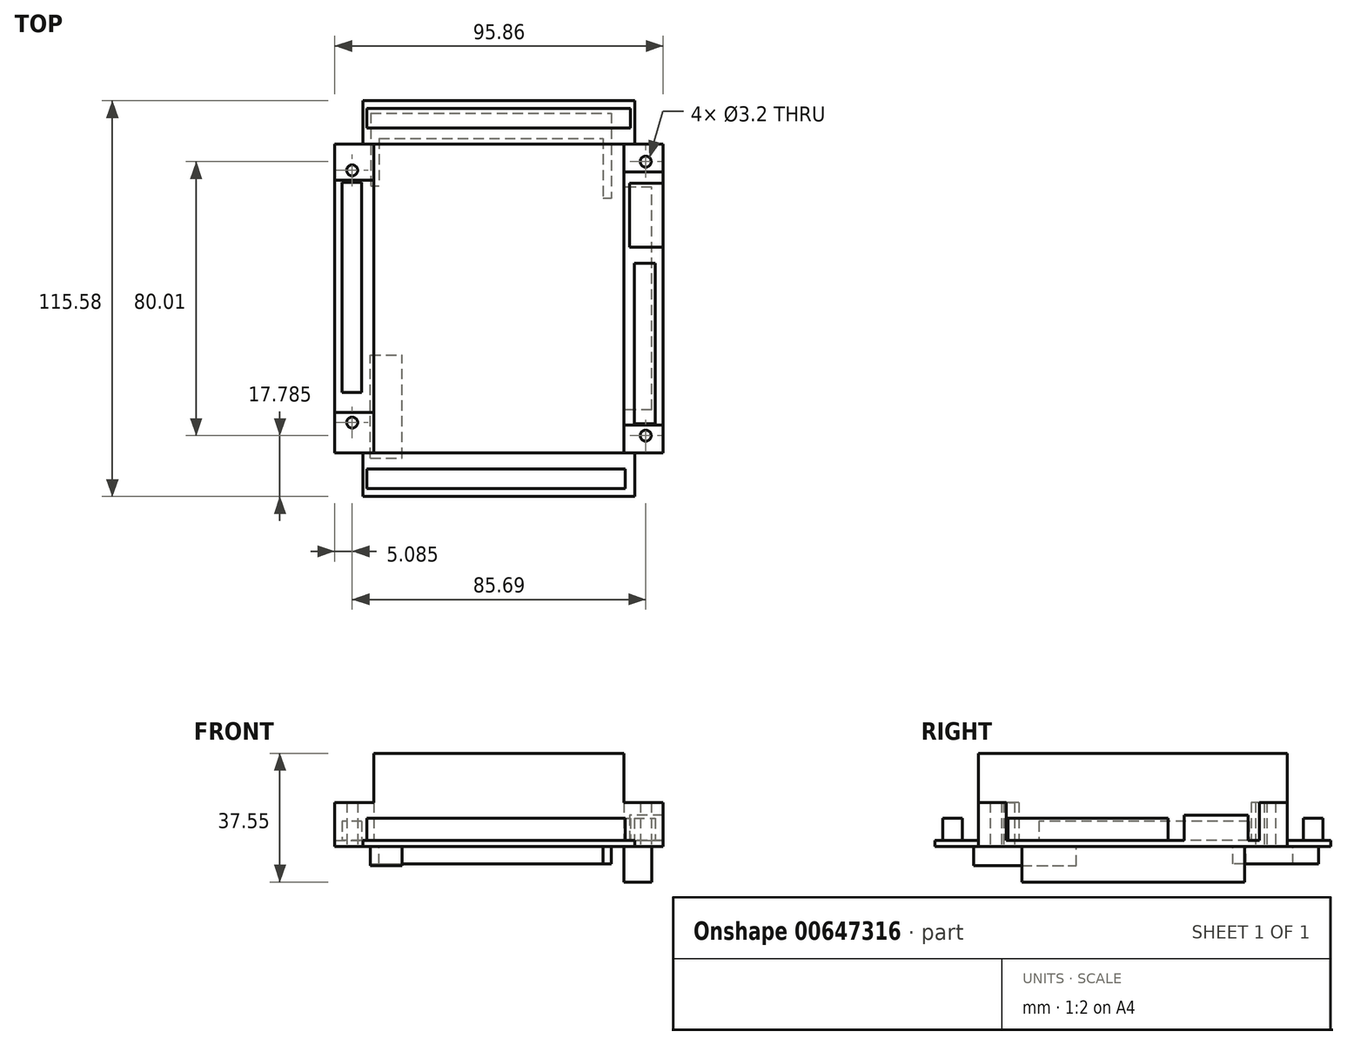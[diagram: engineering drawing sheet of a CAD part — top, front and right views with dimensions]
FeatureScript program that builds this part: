
annotation { "Feature Type Name" : "Feature", "Feature Type Description" : "" }
export const myFeature = defineFeature(function(context is Context, id is Id, definition is map)
    precondition{}
    {
        {
            var Q0;
            Q0=qCreatedBy(makeId("Top.planeOp"),FACE);
            var sketch = newSketch(context, id + "F0", { "sketchPlane" : qUnion([Q0])});
            skLineSegment(sketch, "E0.bottom", {"start": v(47.92, -45.09) * mm, "end": v(-47.92, -45.09) * mm});
            skLineSegment(sketch, "E0.top", {"start": v(47.92, 45.09) * mm, "end": v(-47.92, 45.09) * mm});
            skLineSegment(sketch, "E0.left", {"start": v(47.92, -45.09) * mm, "end": v(47.92, 45.09) * mm});
            skLineSegment(sketch, "E0.right", {"start": v(-47.92, -45.09) * mm, "end": v(-47.92, 45.09) * mm});
            skPoint(sketch, "E0.middle", {"position": v(0, 0) * mm});
            skLineSegment(sketch, "E1.bottom", {"start": v(39.7, -57.78) * mm, "end": v(-39.7, -57.79) * mm});
            skLineSegment(sketch, "E1.top", {"start": v(39.7, 57.78) * mm, "end": v(-39.7, 57.78) * mm});
            skLineSegment(sketch, "E1.left", {"start": v(39.69, -57.79) * mm, "end": v(39.7, 57.78) * mm});
            skLineSegment(sketch, "E1.right", {"start": v(-39.7, -57.79) * mm, "end": v(-39.7, 57.78) * mm});
            skSolve(sketch);
        }
        {
            var Q0;
            Q0 = qSketchRegion(id + "F0", true);
            extrude(context, id + "F1", {"entities" : qUnion([Q0]), "depth" : 1.73 * mm, "offsetDistance" : 25 * mm});
        }
        {
            var Q0;
            Q0=makeQuery(id+"F1.opExtrude","CAP_FACE",FACE,{"disambiguationData":[OSD([sQuery(id+"F0.wireOp",EDGE,"E0.bottom"),sQuery(id+"F0.wireOp",EDGE,"E0.top"),sQuery(id+"F0.wireOp",EDGE,"E0.left"),sQuery(id+"F0.wireOp",EDGE,"E0.right"),sQuery(id+"F0.wireOp",EDGE,"E1.bottom"),sQuery(id+"F0.wireOp",EDGE,"E1.top"),sQuery(id+"F0.wireOp",EDGE,"E1.left"),sQuery(id+"F0.wireOp",EDGE,"E1.right")])],"isStart":true});
            var sketch = newSketch(context, id + "F2", { "sketchPlane" : qUnion([Q0])});
            skLineSegment(sketch, "E2.bottom", {"start": v(44.62, 32.43) * mm, "end": v(36.5, 32.43) * mm});
            skLineSegment(sketch, "E2.top", {"start": v(44.63, -32.59) * mm, "end": v(36.5, -32.59) * mm});
            skLineSegment(sketch, "E2.left", {"start": v(44.62, 32.43) * mm, "end": v(44.62, -32.59) * mm});
            skLineSegment(sketch, "E2.right", {"start": v(36.5, 32.43) * mm, "end": v(36.5, -32.59) * mm});
            skSolve(sketch);
        }
        {
            var Q0;
            Q0 = qSketchRegion(id + "F2", true);
            extrude(context, id + "F3", {"entities" : qUnion([Q0]), "operationType" : NewBodyOperationType.ADD, "depth" : 10.42 * mm, "offsetDistance" : 25 * mm});
        }
        {
            var Q0;
            Q0=makeQuery(id+"F1.opExtrude","CAP_FACE",FACE,{"disambiguationData":[OSD([sQuery(id+"F0.wireOp",EDGE,"E0.bottom"),sQuery(id+"F0.wireOp",EDGE,"E0.top"),sQuery(id+"F0.wireOp",EDGE,"E0.left"),sQuery(id+"F0.wireOp",EDGE,"E0.right"),sQuery(id+"F0.wireOp",EDGE,"E1.bottom"),sQuery(id+"F0.wireOp",EDGE,"E1.top"),sQuery(id+"F0.wireOp",EDGE,"E1.left"),sQuery(id+"F0.wireOp",EDGE,"E1.right")])],"isStart":true});
            var sketch = newSketch(context, id + "F4", { "sketchPlane" : qUnion([Q0])});
            skLineSegment(sketch, "E3.bottom", {"start": v(-37.4, -46.75) * mm, "end": v(32.8, -46.75) * mm});
            skLineSegment(sketch, "E3.top", {"start": v(-37.4, -54.2) * mm, "end": v(32.8, -54.2) * mm});
            skLineSegment(sketch, "E3.left", {"start": v(-37.4, -46.75) * mm, "end": v(-37.4, -54.2) * mm});
            skLineSegment(sketch, "E3.right", {"start": v(32.8, -46.75) * mm, "end": v(32.8, -54.2) * mm});
            skLineSegment(sketch, "E4.bottom", {"start": v(-37.4, -54.2) * mm, "end": v(-35.02, -54.2) * mm});
            skLineSegment(sketch, "E4.top", {"start": v(-37.4, -32.95) * mm, "end": v(-35.02, -32.95) * mm});
            skLineSegment(sketch, "E4.left", {"start": v(-37.4, -54.2) * mm, "end": v(-37.4, -32.95) * mm});
            skLineSegment(sketch, "E4.right", {"start": v(-35.02, -54.2) * mm, "end": v(-35.02, -32.95) * mm});
            skLineSegment(sketch, "E5.bottom", {"start": v(32.8, -54.2) * mm, "end": v(30.42, -54.2) * mm});
            skLineSegment(sketch, "E5.top", {"start": v(32.8, -29.2) * mm, "end": v(30.42, -29.2) * mm});
            skLineSegment(sketch, "E5.left", {"start": v(32.8, -54.2) * mm, "end": v(32.8, -29.2) * mm});
            skLineSegment(sketch, "E5.right", {"start": v(30.42, -54.2) * mm, "end": v(30.42, -29.2) * mm});
            skSolve(sketch);
        }
        {
            var Q0;
            Q0 = qSketchRegion(id + "F4", true);
            extrude(context, id + "F5", {"entities" : qUnion([Q0]), "operationType" : NewBodyOperationType.ADD, "depth" : 5.18 * mm, "offsetDistance" : 25 * mm});
        }
        {
            var Q0;
            Q0=makeQuery(id+"F1.opExtrude","CAP_FACE",FACE,{"disambiguationData":[OSD([sQuery(id+"F0.wireOp",EDGE,"E0.bottom"),sQuery(id+"F0.wireOp",EDGE,"E0.top"),sQuery(id+"F0.wireOp",EDGE,"E0.left"),sQuery(id+"F0.wireOp",EDGE,"E0.right"),sQuery(id+"F0.wireOp",EDGE,"E1.bottom"),sQuery(id+"F0.wireOp",EDGE,"E1.top"),sQuery(id+"F0.wireOp",EDGE,"E1.left"),sQuery(id+"F0.wireOp",EDGE,"E1.right")])],"isStart":true});
            var sketch = newSketch(context, id + "F6", { "sketchPlane" : qUnion([Q0])});
            skLineSegment(sketch, "E6.bottom", {"start": v(-37.57, 46.5) * mm, "end": v(-28.27, 46.5) * mm});
            skLineSegment(sketch, "E6.top", {"start": v(-37.57, 16.5) * mm, "end": v(-28.27, 16.5) * mm});
            skLineSegment(sketch, "E6.left", {"start": v(-37.57, 46.5) * mm, "end": v(-37.57, 16.5) * mm});
            skLineSegment(sketch, "E6.right", {"start": v(-28.27, 46.5) * mm, "end": v(-28.27, 16.5) * mm});
            skSolve(sketch);
        }
        {
            var Q0;
            Q0 = qSketchRegion(id + "F6", true);
            extrude(context, id + "F7", {"entities" : qUnion([Q0]), "operationType" : NewBodyOperationType.ADD, "depth" : 5.58 * mm, "offsetDistance" : 25 * mm});
        }
        {
            var Q0;
            Q0=makeQuery(id+"F1.opExtrude","CAP_FACE",FACE,{"disambiguationData":[OSD([sQuery(id+"F0.wireOp",EDGE,"E0.bottom"),sQuery(id+"F0.wireOp",EDGE,"E0.top"),sQuery(id+"F0.wireOp",EDGE,"E0.left"),sQuery(id+"F0.wireOp",EDGE,"E0.right"),sQuery(id+"F0.wireOp",EDGE,"E1.bottom"),sQuery(id+"F0.wireOp",EDGE,"E1.top"),sQuery(id+"F0.wireOp",EDGE,"E1.left"),sQuery(id+"F0.wireOp",EDGE,"E1.right")])],"isStart":false});
            var sketch = newSketch(context, id + "F8", { "sketchPlane" : qUnion([Q0])});
            skLineSegment(sketch, "E7.bottom", {"start": v(36.52, 45.08) * mm, "end": v(-36.52, 45.08) * mm});
            skLineSegment(sketch, "E7.top", {"start": v(36.52, -45.09) * mm, "end": v(-36.52, -45.09) * mm});
            skLineSegment(sketch, "E7.left", {"start": v(36.52, 45.08) * mm, "end": v(36.52, -45.09) * mm});
            skLineSegment(sketch, "E7.right", {"start": v(-36.52, 45.08) * mm, "end": v(-36.52, -45.09) * mm});
            skPoint(sketch, "E7.middle", {"position": v(0, 0) * mm});
            skSolve(sketch);
        }
        {
            var Q0;
            Q0 = qSketchRegion(id + "F8", true);
            extrude(context, id + "F9", {"entities" : qUnion([Q0]), "operationType" : NewBodyOperationType.ADD, "depth" : 25.4 * mm, "offsetDistance" : 25 * mm});
        }
        {
            var Q0;
            Q0=makeQuery(id+"F1.opExtrude","CAP_FACE",FACE,{"disambiguationData":[OSD([sQuery(id+"F0.wireOp",EDGE,"E0.bottom"),sQuery(id+"F0.wireOp",EDGE,"E0.top"),sQuery(id+"F0.wireOp",EDGE,"E0.left"),sQuery(id+"F0.wireOp",EDGE,"E0.right"),sQuery(id+"F0.wireOp",EDGE,"E1.bottom"),sQuery(id+"F0.wireOp",EDGE,"E1.top"),sQuery(id+"F0.wireOp",EDGE,"E1.left"),sQuery(id+"F0.wireOp",EDGE,"E1.right")])],"isStart":false});
            var sketch = newSketch(context, id + "F10", { "sketchPlane" : qUnion([Q0])});
            skLineSegment(sketch, "E8.bottom", {"start": v(36.52, 45.08) * mm, "end": v(47.92, 45.08) * mm});
            skLineSegment(sketch, "E8.top", {"start": v(36.52, 36.95) * mm, "end": v(47.92, 36.95) * mm});
            skLineSegment(sketch, "E8.left", {"start": v(36.52, 45.08) * mm, "end": v(36.52, 36.95) * mm});
            skLineSegment(sketch, "E8.right", {"start": v(47.92, 45.08) * mm, "end": v(47.92, 36.95) * mm});
            skLineSegment(sketch, "E9.bottom", {"start": v(36.52, -45.09) * mm, "end": v(47.92, -45.09) * mm});
            skLineSegment(sketch, "E9.top", {"start": v(36.52, -36.95) * mm, "end": v(47.92, -36.95) * mm});
            skLineSegment(sketch, "E9.left", {"start": v(36.52, -45.09) * mm, "end": v(36.52, -36.95) * mm});
            skLineSegment(sketch, "E9.right", {"start": v(47.92, -45.09) * mm, "end": v(47.92, -36.95) * mm});
            skLineSegment(sketch, "E10.bottom", {"start": v(-36.52, 45.08) * mm, "end": v(-47.92, 45.08) * mm});
            skLineSegment(sketch, "E10.top", {"start": v(-36.52, 34.55) * mm, "end": v(-47.92, 34.55) * mm});
            skLineSegment(sketch, "E10.left", {"start": v(-36.52, 45.08) * mm, "end": v(-36.52, 34.55) * mm});
            skLineSegment(sketch, "E10.right", {"start": v(-47.92, 45.08) * mm, "end": v(-47.92, 34.55) * mm});
            skLineSegment(sketch, "E11.bottom", {"start": v(-47.92, -45.09) * mm, "end": v(-36.52, -45.09) * mm});
            skLineSegment(sketch, "E11.top", {"start": v(-47.92, -33.28) * mm, "end": v(-36.52, -33.28) * mm});
            skLineSegment(sketch, "E11.left", {"start": v(-47.92, -45.09) * mm, "end": v(-47.92, -33.28) * mm});
            skLineSegment(sketch, "E11.right", {"start": v(-36.52, -45.09) * mm, "end": v(-36.52, -33.28) * mm});
            skSolve(sketch);
        }
        {
            var Q0;
            Q0 = qSketchRegion(id + "F10", true);
            extrude(context, id + "F11", {"entities" : qUnion([Q0]), "operationType" : NewBodyOperationType.ADD, "depth" : 11.1 * mm, "offsetDistance" : 25 * mm});
        }
        {
            var Q0;
            {var subQ0=sQuery(id+"F0.wireOp",EDGE,"E1.bottom");var subQ1=sQuery(id+"F0.wireOp",EDGE,"E0.right");var subQ2=sQuery(id+"F0.wireOp",EDGE,"E0.bottom");var subQ3=sQuery(id+"F0.wireOp",EDGE,"E1.right");var subQ5=sQuery(id+"F0.wireOp",EDGE,"E1.left");var subQ7=sQuery(id+"F0.wireOp",EDGE,"E0.left");Q0=makeQuery(id+"F11.boolean.opBoolean","SPLIT",FACE,{"disambiguationData":[TD([makeQuery(id+"F1.opExtrude","SWEPT_FACE",FACE,{"disambiguationData":[OSD([subQ0])]})])],"derivedFrom":makeQuery(id+"F1.opExtrude","CAP_FACE",FACE,{"disambiguationData":[OSD([subQ2,sQuery(id+"F0.wireOp",EDGE,"E0.top"),subQ7,subQ1,subQ0,sQuery(id+"F0.wireOp",EDGE,"E1.top"),subQ5,subQ3])],"isStart":false})});}
            var sketch = newSketch(context, id + "F12", { "sketchPlane" : qUnion([Q0])});
            skLineSegment(sketch, "E12.bottom", {"start": v(-38.63, -55.5) * mm, "end": v(36.88, -55.5) * mm});
            skLineSegment(sketch, "E12.top", {"start": v(-38.63, -49.76) * mm, "end": v(36.88, -49.75) * mm});
            skLineSegment(sketch, "E12.left", {"start": v(-38.63, -55.5) * mm, "end": v(-38.63, -49.76) * mm});
            skLineSegment(sketch, "E12.right", {"start": v(36.88, -55.5) * mm, "end": v(36.88, -49.75) * mm});
            skSolve(sketch);
        }
        {
            var Q0;
            Q0 = qSketchRegion(id + "F12", true);
            extrude(context, id + "F13", {"entities" : qUnion([Q0]), "operationType" : NewBodyOperationType.ADD, "depth" : 6.43 * mm, "offsetDistance" : 25 * mm});
        }
        {
            var Q0;
            {var subQ0=sQuery(id+"F0.wireOp",EDGE,"E0.right");Q0=makeQuery(id+"F11.boolean.opBoolean","SPLIT",FACE,{"disambiguationData":[TD([makeQuery(id+"F1.opExtrude","SWEPT_FACE",FACE,{"disambiguationData":[OSD([subQ0])]})])],"derivedFrom":makeQuery(id+"F1.opExtrude","CAP_FACE",FACE,{"disambiguationData":[OSD([sQuery(id+"F0.wireOp",EDGE,"E0.bottom"),sQuery(id+"F0.wireOp",EDGE,"E0.top"),sQuery(id+"F0.wireOp",EDGE,"E0.left"),subQ0,sQuery(id+"F0.wireOp",EDGE,"E1.bottom"),sQuery(id+"F0.wireOp",EDGE,"E1.top"),sQuery(id+"F0.wireOp",EDGE,"E1.left"),sQuery(id+"F0.wireOp",EDGE,"E1.right")])],"isStart":false})});}
            var sketch = newSketch(context, id + "F14", { "sketchPlane" : qUnion([Q0])});
            skLineSegment(sketch, "E13.bottom", {"start": v(-40.05, 33.94) * mm, "end": v(-45.78, 33.94) * mm});
            skLineSegment(sketch, "E13.top", {"start": v(-40.05, -27.45) * mm, "end": v(-45.77, -27.45) * mm});
            skLineSegment(sketch, "E13.left", {"start": v(-40.05, 33.94) * mm, "end": v(-40.05, -27.45) * mm});
            skLineSegment(sketch, "E13.right", {"start": v(-45.78, 33.94) * mm, "end": v(-45.77, -27.45) * mm});
            skSolve(sketch);
        }
        {
            var Q0;
            Q0 = qSketchRegion(id + "F14", true);
            extrude(context, id + "F15", {"entities" : qUnion([Q0]), "operationType" : NewBodyOperationType.ADD, "depth" : 5.57 * mm, "offsetDistance" : 25 * mm});
        }
        {
            var Q0;
            {var subQ0=sQuery(id+"F0.wireOp",EDGE,"E1.left");var subQ1=sQuery(id+"F0.wireOp",EDGE,"E1.top");var subQ2=sQuery(id+"F0.wireOp",EDGE,"E0.top");var subQ4=sQuery(id+"F0.wireOp",EDGE,"E0.right");var subQ5=sQuery(id+"F0.wireOp",EDGE,"E1.right");var subQ7=sQuery(id+"F0.wireOp",EDGE,"E0.left");Q0=makeQuery(id+"F11.boolean.opBoolean","SPLIT",FACE,{"disambiguationData":[TD([makeQuery(id+"F1.opExtrude","SWEPT_FACE",FACE,{"disambiguationData":[OSD([subQ1])]})])],"derivedFrom":makeQuery(id+"F1.opExtrude","CAP_FACE",FACE,{"disambiguationData":[OSD([sQuery(id+"F0.wireOp",EDGE,"E0.bottom"),subQ2,subQ7,subQ4,sQuery(id+"F0.wireOp",EDGE,"E1.bottom"),subQ1,subQ0,subQ5])],"isStart":false})});}
            var sketch = newSketch(context, id + "F16", { "sketchPlane" : qUnion([Q0])});
            skLineSegment(sketch, "E14.bottom", {"start": v(-38.63, 49.8) * mm, "end": v(38.44, 49.8) * mm});
            skLineSegment(sketch, "E14.top", {"start": v(-38.63, 55.54) * mm, "end": v(38.44, 55.54) * mm});
            skLineSegment(sketch, "E14.left", {"start": v(-38.63, 49.8) * mm, "end": v(-38.63, 55.54) * mm});
            skLineSegment(sketch, "E14.right", {"start": v(38.44, 49.8) * mm, "end": v(38.44, 55.54) * mm});
            skSolve(sketch);
        }
        {
            var Q0;
            Q0 = qSketchRegion(id + "F16", true);
            extrude(context, id + "F17", {"entities" : qUnion([Q0]), "operationType" : NewBodyOperationType.ADD, "depth" : 6.43 * mm, "offsetDistance" : 25 * mm});
        }
        {
            var Q0;
            {var subQ0=sQuery(id+"F0.wireOp",EDGE,"E0.left");Q0=makeQuery(id+"F11.boolean.opBoolean","SPLIT",FACE,{"disambiguationData":[TD([makeQuery(id+"F1.opExtrude","SWEPT_FACE",FACE,{"disambiguationData":[OSD([subQ0])]})])],"derivedFrom":makeQuery(id+"F1.opExtrude","CAP_FACE",FACE,{"disambiguationData":[OSD([sQuery(id+"F0.wireOp",EDGE,"E0.bottom"),sQuery(id+"F0.wireOp",EDGE,"E0.top"),subQ0,sQuery(id+"F0.wireOp",EDGE,"E0.right"),sQuery(id+"F0.wireOp",EDGE,"E1.bottom"),sQuery(id+"F0.wireOp",EDGE,"E1.top"),sQuery(id+"F0.wireOp",EDGE,"E1.left"),sQuery(id+"F0.wireOp",EDGE,"E1.right")])],"isStart":false})});}
            var sketch = newSketch(context, id + "F18", { "sketchPlane" : qUnion([Q0])});
            skLineSegment(sketch, "E15.bottom", {"start": v(39.47, 10.34) * mm, "end": v(45.64, 10.34) * mm});
            skLineSegment(sketch, "E15.top", {"start": v(39.47, -36.48) * mm, "end": v(45.64, -36.48) * mm});
            skLineSegment(sketch, "E15.left", {"start": v(39.47, 10.35) * mm, "end": v(39.47, -36.48) * mm});
            skLineSegment(sketch, "E15.right", {"start": v(45.64, 10.35) * mm, "end": v(45.64, -36.48) * mm});
            skSolve(sketch);
        }
        {
            var Q0;
            Q0 = qSketchRegion(id + "F18", true);
            extrude(context, id + "F19", {"entities" : qUnion([Q0]), "operationType" : NewBodyOperationType.ADD, "depth" : 6.43 * mm, "offsetDistance" : 25 * mm});
        }
        {
            var Q0;
            {var subQ0=sQuery(id+"F0.wireOp",EDGE,"E0.left");Q0=makeQuery(id+"F11.boolean.opBoolean","SPLIT",FACE,{"disambiguationData":[TD([makeQuery(id+"F1.opExtrude","SWEPT_FACE",FACE,{"disambiguationData":[OSD([subQ0])]})])],"derivedFrom":makeQuery(id+"F1.opExtrude","CAP_FACE",FACE,{"disambiguationData":[OSD([sQuery(id+"F0.wireOp",EDGE,"E0.bottom"),sQuery(id+"F0.wireOp",EDGE,"E0.top"),subQ0,sQuery(id+"F0.wireOp",EDGE,"E0.right"),sQuery(id+"F0.wireOp",EDGE,"E1.bottom"),sQuery(id+"F0.wireOp",EDGE,"E1.top"),sQuery(id+"F0.wireOp",EDGE,"E1.left"),sQuery(id+"F0.wireOp",EDGE,"E1.right")])],"isStart":false})});}
            var sketch = newSketch(context, id + "F20", { "sketchPlane" : qUnion([Q0])});
            skLineSegment(sketch, "E16.bottom", {"start": v(47.92, 33.68) * mm, "end": v(38.14, 33.68) * mm});
            skLineSegment(sketch, "E16.top", {"start": v(47.92, 15.03) * mm, "end": v(38.14, 15.03) * mm});
            skLineSegment(sketch, "E16.left", {"start": v(47.92, 33.68) * mm, "end": v(47.92, 15.03) * mm});
            skLineSegment(sketch, "E16.right", {"start": v(38.14, 33.68) * mm, "end": v(38.14, 15.03) * mm});
            skSolve(sketch);
        }
        {
            var Q0;
            Q0 = qSketchRegion(id + "F20", true);
            extrude(context, id + "F21", {"entities" : qUnion([Q0]), "operationType" : NewBodyOperationType.ADD, "depth" : 7.35 * mm, "offsetDistance" : 25 * mm});
        }
        {
            var Q0;
            Q0=makeQuery(id+"F1.opExtrude","CAP_FACE",FACE,{"disambiguationData":[OSD([sQuery(id+"F0.wireOp",EDGE,"E0.bottom"),sQuery(id+"F0.wireOp",EDGE,"E0.top"),sQuery(id+"F0.wireOp",EDGE,"E0.left"),sQuery(id+"F0.wireOp",EDGE,"E0.right"),sQuery(id+"F0.wireOp",EDGE,"E1.bottom"),sQuery(id+"F0.wireOp",EDGE,"E1.top"),sQuery(id+"F0.wireOp",EDGE,"E1.left"),sQuery(id+"F0.wireOp",EDGE,"E1.right")])],"isStart":true});
            var sketch = newSketch(context, id + "F22", { "sketchPlane" : qUnion([Q0])});
            skCircle(sketch, "E17", {"center": v(42.84, 40) * mm, "radius": 1.6 * mm});
            skCircle(sketch, "E18", {"center": v(42.84, -40) * mm, "radius": 1.6 * mm});
            skCircle(sketch, "E19", {"center": v(-42.84, -37.46) * mm, "radius": 1.6 * mm});
            skCircle(sketch, "E20", {"center": v(-42.84, 36.19) * mm, "radius": 1.6 * mm});
            skSolve(sketch);
        }
        {
            var Q0;
            Q0 = qSketchRegion(id + "F22", true);
            extrude(context, id + "F23", {"entities" : qUnion([Q0]), "operationType" : NewBodyOperationType.REMOVE, "endBound" : BoundingType.THROUGH_ALL, "oppositeDirection" : true, "depth" : 25 * mm, "offsetDistance" : 25 * mm});
        }
    });
